annotation { "Feature Type Name" : "Feature", "Feature Type Description" : "" }
export const myFeature = defineFeature(function(context is Context, id is Id, definition is map)
    precondition{}
    {
        {
            var Q0;
            Q0=qCreatedBy(makeId("Top.planeOp"),FACE);
            var sketch = newSketch(context, id + "F0", { "sketchPlane" : qUnion([Q0])});
            skLineSegment(sketch, "E0.bottom", {"start": v(112.5, -12.5) * mm, "end": v(-112.5, -12.5) * mm});
            skLineSegment(sketch, "E0.top", {"start": v(112.5, 12.5) * mm, "end": v(-112.5, 12.5) * mm});
            skLineSegment(sketch, "E0.left", {"start": v(112.5, -12.5) * mm, "end": v(112.5, 12.5) * mm});
            skLineSegment(sketch, "E0.right", {"start": v(-112.5, -12.5) * mm, "end": v(-112.5, 12.5) * mm});
            skText(sketch, "E1", { "text": "Joseph Schmitz", "fontName": "RobotoSlab-Bold.ttf"});
            skPoint(sketch, "E2", {"position": v(-34.31, 0) * mm});
            skPoint(sketch, "E3", {"position": v(0, -12.5) * mm});
            skLineSegment(sketch, "E4", {"start": v(91.36, 3.09) * mm, "end": v(97.96, 10.26) * mm});
            skLineSegment(sketch, "E5", {"start": v(97.96, 10.26) * mm, "end": v(96.05, 3.1) * mm});
            skLineSegment(sketch, "E6", {"start": v(96.05, 3.1) * mm, "end": v(104.2, 3.1) * mm});
            skLineSegment(sketch, "E7", {"start": v(104.2, 3.1) * mm, "end": v(94.83, -1.5) * mm});
            skLineSegment(sketch, "E8", {"start": v(94.43, -1.04) * mm, "end": v(95.04, 2.05) * mm});
            skLineSegment(sketch, "E9", {"start": v(95.04, 2.05) * mm, "end": v(91.13, 2.15) * mm});
            skLineSegment(sketch, "E10", {"start": v(95.94, 6.62) * mm, "end": v(95.24, 3.1) * mm});
            skLineSegment(sketch, "E11", {"start": v(95.24, 3.1) * mm, "end": v(92.14, 3.09) * mm});
            skLineSegment(sketch, "E12", {"start": v(92.14, 3.09) * mm, "end": v(95.94, 6.62) * mm});
            skLineSegment(sketch, "E13", {"start": v(95.77, 2.03) * mm, "end": v(99.85, 1.91) * mm});
            skLineSegment(sketch, "E14", {"start": v(99.85, 1.91) * mm, "end": v(95.05, -0.7) * mm});
            skLineSegment(sketch, "E15", {"start": v(95.05, -0.7) * mm, "end": v(95.77, 2.03) * mm});
            skLineSegment(sketch, "E16", {"start": v(97.96, 10.26) * mm, "end": v(95.94, 6.62) * mm, "construction": true});
            skText(sketch, "E17", { "text": "121-D", "fontName": "RobotoSlab-Bold.ttf"});
            skPoint(sketch, "E18", {"position": v(92.9, -8.75) * mm});
            skPoint(sketch, "E19", {"position": v(81.54, -8.05) * mm});
            skPoint(sketch, "E20", {"position": v(86.8, -1.87) * mm});
            skPoint(sketch, "E21", {"position": v(59.08, 3.04) * mm});
            skLineSegment(sketch, "E22", {"start": v(94.83, -1.5) * mm, "end": v(92.9, -8.75) * mm});
            skLineSegment(sketch, "E23", {"start": v(94.43, -1.04) * mm, "end": v(81.54, -8.05) * mm});
            skLineSegment(sketch, "E24", {"start": v(86.8, -1.87) * mm, "end": v(91.13, 2.15) * mm});
            skLineSegment(sketch, "E25", {"start": v(59.08, 3.04) * mm, "end": v(91.36, 3.09) * mm});
            skLineSegment(sketch, "E26", {"start": v(59.08, 3.04) * mm, "end": v(59.07, 2.64) * mm});
            skLineSegment(sketch, "E27", {"start": v(59.07, 2.64) * mm, "end": v(90.4, 2.15) * mm});
            skLineSegment(sketch, "E28", {"start": v(86.8, -1.87) * mm, "end": v(86.53, -1.58) * mm});
            skLineSegment(sketch, "E29", {"start": v(86.53, -1.58) * mm, "end": v(91.36, 3.09) * mm, "construction": true});
            skLineSegment(sketch, "E30", {"start": v(86.53, -1.58) * mm, "end": v(90.4, 2.15) * mm});
            skLineSegment(sketch, "E31", {"start": v(81.54, -8.05) * mm, "end": v(81.73, -8.4) * mm});
            skLineSegment(sketch, "E32", {"start": v(92.9, -8.75) * mm, "end": v(92.52, -8.65) * mm});
            skLineSegment(sketch, "E33", {"start": v(81.73, -8.4) * mm, "end": v(94.83, -1.5) * mm, "construction": true});
            skLineSegment(sketch, "E34", {"start": v(92.52, -8.65) * mm, "end": v(94.43, -1.04) * mm, "construction": true});
            skLineSegment(sketch, "E35", {"start": v(81.73, -8.4) * mm, "end": v(94.23, -1.82) * mm});
            skLineSegment(sketch, "E36", {"start": v(94.23, -1.82) * mm, "end": v(92.52, -8.65) * mm});
            const initialGuessF0  = {"E1": [-0.1025, -0.0065, 1, 0, 0.013], "E17": [0.04787, -0.0095, 1, 0, 0.009]};
            skSetInitialGuess(sketch, initialGuessF0);
            skSolve(sketch);
        }
        {
            var Q0;
            Q0=makeQuery(id+"F0.imprint","IMPRINT",FACE,{"disambiguationData":[TD([[makeQuery(id+"F0.imprint","IMPRINT",EDGE,{"derivedFrom":sQuery(id+"F0.wireOp",EDGE,"E0.bottom")}),-1.0]])]});
            var Q1;
            Q1=makeQuery(id+"F0.imprint","IMPRINT",FACE,{"disambiguationData":[TD([[makeQuery(id+"F0.imprint","IMPRINT",EDGE,{"derivedFrom":sQuery(id+"F0.wireOp",EDGE,"E1.sketch_text.stroke-112")}),1.0]])]});
            var Q2;
            Q2=makeQuery(id+"F0.imprint","IMPRINT",FACE,{"disambiguationData":[TD([[makeQuery(id+"F0.imprint","IMPRINT",EDGE,{"derivedFrom":sQuery(id+"F0.wireOp",EDGE,"E1.sketch_text.stroke-85")}),1.0]])]});
            var Q3;
            Q3=makeQuery(id+"F0.imprint","IMPRINT",FACE,{"disambiguationData":[TD([[makeQuery(id+"F0.imprint","IMPRINT",EDGE,{"derivedFrom":sQuery(id+"F0.wireOp",EDGE,"E1.sketch_text.stroke-28")}),1.0]])]});
            var Q4;
            Q4=makeQuery(id+"F0.imprint","IMPRINT",FACE,{"disambiguationData":[TD([[makeQuery(id+"F0.imprint","IMPRINT",EDGE,{"derivedFrom":sQuery(id+"F0.wireOp",EDGE,"E13")}),-1.0]])]});
            var Q5;
            Q5=makeQuery(id+"F0.imprint","IMPRINT",FACE,{"disambiguationData":[TD([[makeQuery(id+"F0.imprint","IMPRINT",EDGE,{"derivedFrom":sQuery(id+"F0.wireOp",EDGE,"E10")}),-1.0]])]});
            var Q6;
            Q6=makeQuery(id+"F0.imprint","IMPRINT",FACE,{"disambiguationData":[TD([[makeQuery(id+"F0.imprint","IMPRINT",EDGE,{"derivedFrom":sQuery(id+"F0.wireOp",EDGE,"E17.sketch_text.stroke-60")}),1.0]])]});
            extrude(context, id + "F1", {"entities" : qUnion([Q0, Q1, Q2, Q3, Q4, Q5, Q6]), "depth" : (0.3 + .2 + .2) * mm});
        }
        {
            var Q0;
            Q0=makeQuery(id+"F0.imprint","IMPRINT",FACE,{"disambiguationData":[TD([[makeQuery(id+"F0.imprint","IMPRINT",EDGE,{"derivedFrom":sQuery(id+"F0.wireOp",EDGE,"E1.sketch_text.stroke-227")}),-1.0]])]});
            var Q1;
            Q1=makeQuery(id+"F0.imprint","IMPRINT",FACE,{"disambiguationData":[TD([[makeQuery(id+"F0.imprint","IMPRINT",EDGE,{"derivedFrom":sQuery(id+"F0.wireOp",EDGE,"E1.sketch_text.stroke-280")}),-1.0]])]});
            var Q2;
            Q2=makeQuery(id+"F0.imprint","IMPRINT",FACE,{"disambiguationData":[TD([[makeQuery(id+"F0.imprint","IMPRINT",EDGE,{"derivedFrom":sQuery(id+"F0.wireOp",EDGE,"E1.sketch_text.stroke-270")}),-1.0]])]});
            var Q3;
            Q3=makeQuery(id+"F0.imprint","IMPRINT",FACE,{"disambiguationData":[TD([[makeQuery(id+"F0.imprint","IMPRINT",EDGE,{"derivedFrom":sQuery(id+"F0.wireOp",EDGE,"E1.sketch_text.stroke-284")}),-1.0]])]});
            var Q4;
            Q4=makeQuery(id+"F0.imprint","IMPRINT",FACE,{"disambiguationData":[TD([[makeQuery(id+"F0.imprint","IMPRINT",EDGE,{"derivedFrom":sQuery(id+"F0.wireOp",EDGE,"E1.sketch_text.stroke-304")}),-1.0]])]});
            var Q5;
            Q5=makeQuery(id+"F0.imprint","IMPRINT",FACE,{"disambiguationData":[TD([[makeQuery(id+"F0.imprint","IMPRINT",EDGE,{"derivedFrom":sQuery(id+"F0.wireOp",EDGE,"E17.sketch_text.stroke-0")}),-1.0]])]});
            var Q6;
            Q6=makeQuery(id+"F0.imprint","IMPRINT",FACE,{"disambiguationData":[TD([[makeQuery(id+"F0.imprint","IMPRINT",EDGE,{"derivedFrom":sQuery(id+"F0.wireOp",EDGE,"E17.sketch_text.stroke-10")}),-1.0]])]});
            var Q7;
            Q7=makeQuery(id+"F0.imprint","IMPRINT",FACE,{"disambiguationData":[TD([[makeQuery(id+"F0.imprint","IMPRINT",EDGE,{"derivedFrom":sQuery(id+"F0.wireOp",EDGE,"E17.sketch_text.stroke-33")}),-1.0]])]});
            var Q8;
            Q8=makeQuery(id+"F0.imprint","IMPRINT",FACE,{"disambiguationData":[TD([[makeQuery(id+"F0.imprint","IMPRINT",EDGE,{"derivedFrom":sQuery(id+"F0.wireOp",EDGE,"E17.sketch_text.stroke-43")}),-1.0]])]});
            var Q9;
            Q9=makeQuery(id+"F0.imprint","IMPRINT",FACE,{"disambiguationData":[TD([[makeQuery(id+"F0.imprint","IMPRINT",EDGE,{"derivedFrom":sQuery(id+"F0.wireOp",EDGE,"E17.sketch_text.stroke-47")}),-1.0]])]});
            var Q10;
            Q10=makeQuery(id+"F0.imprint","IMPRINT",FACE,{"disambiguationData":[TD([[makeQuery(id+"F0.imprint","IMPRINT",EDGE,{"derivedFrom":sQuery(id+"F0.wireOp",EDGE,"66f59e6f-d666-4f71-bfd4-2eef0c262501")}),-1.0]])]});
            var Q11;
            Q11=makeQuery(id+"F0.imprint","IMPRINT",FACE,{"disambiguationData":[TD([[makeQuery(id+"F0.imprint","IMPRINT",EDGE,{"derivedFrom":sQuery(id+"F0.wireOp",EDGE,"E1.sketch_text.stroke-0")}),-1.0]])]});
            var Q12;
            Q12=makeQuery(id+"F0.imprint","IMPRINT",FACE,{"disambiguationData":[TD([[makeQuery(id+"F0.imprint","IMPRINT",EDGE,{"derivedFrom":sQuery(id+"F0.wireOp",EDGE,"E1.sketch_text.stroke-18")}),-1.0]])]});
            var Q13;
            Q13=makeQuery(id+"F0.imprint","IMPRINT",FACE,{"disambiguationData":[TD([[makeQuery(id+"F0.imprint","IMPRINT",EDGE,{"derivedFrom":sQuery(id+"F0.wireOp",EDGE,"E1.sketch_text.stroke-38")}),-1.0]])]});
            var Q14;
            Q14=makeQuery(id+"F0.imprint","IMPRINT",FACE,{"disambiguationData":[TD([[makeQuery(id+"F0.imprint","IMPRINT",EDGE,{"derivedFrom":sQuery(id+"F0.wireOp",EDGE,"E1.sketch_text.stroke-68")}),-1.0]])]});
            var Q15;
            Q15=makeQuery(id+"F0.imprint","IMPRINT",FACE,{"disambiguationData":[TD([[makeQuery(id+"F0.imprint","IMPRINT",EDGE,{"derivedFrom":sQuery(id+"F0.wireOp",EDGE,"E1.sketch_text.stroke-92")}),-1.0]])]});
            var Q16;
            Q16=makeQuery(id+"F0.imprint","IMPRINT",FACE,{"disambiguationData":[TD([[makeQuery(id+"F0.imprint","IMPRINT",EDGE,{"derivedFrom":sQuery(id+"F0.wireOp",EDGE,"E1.sketch_text.stroke-122")}),-1.0]])]});
            var Q17;
            Q17=makeQuery(id+"F0.imprint","IMPRINT",FACE,{"disambiguationData":[TD([[makeQuery(id+"F0.imprint","IMPRINT",EDGE,{"derivedFrom":sQuery(id+"F0.wireOp",EDGE,"E1.sketch_text.stroke-148")}),-1.0]])]});
            var Q18;
            Q18=makeQuery(id+"F0.imprint","IMPRINT",FACE,{"disambiguationData":[TD([[makeQuery(id+"F0.imprint","IMPRINT",EDGE,{"derivedFrom":sQuery(id+"F0.wireOp",EDGE,"E1.sketch_text.stroke-178")}),-1.0]])]});
            var Q19;
            Q19=makeQuery(id+"F0.imprint","IMPRINT",FACE,{"disambiguationData":[TD([[makeQuery(id+"F0.imprint","IMPRINT",EDGE,{"derivedFrom":sQuery(id+"F0.wireOp",EDGE,"E1.sketch_text.stroke-201")}),-1.0]])]});
            var Q20;
            Q20=makeQuery(id+"F0.imprint","IMPRINT",FACE,{"disambiguationData":[TD([[makeQuery(id+"F0.imprint","IMPRINT",EDGE,{"derivedFrom":sQuery(id+"F0.wireOp",EDGE,"E4")}),-1.0]])]});
            extrude(context, id + "F2", {"entities" : qUnion([Q0, Q1, Q2, Q3, Q4, Q5, Q6, Q7, Q8, Q9, Q10, Q11, Q12, Q13, Q14, Q15, Q16, Q17, Q18, Q19, Q20]), "depth" : 8 * mm});
        }
        {
            var Q0;
            Q0=qCreatedBy(makeId("Top.planeOp"),FACE);
            var sketch = newSketch(context, id + "F3", { "sketchPlane" : qUnion([Q0])});
            skLineSegment(sketch, "E37.bottom", {"start": v(-112.5, 12.5) * mm, "end": v(-37.5, 12.5) * mm});
            skLineSegment(sketch, "E37.top", {"start": v(-112.5, -12.5) * mm, "end": v(-37.5, -12.5) * mm});
            skLineSegment(sketch, "E37.left", {"start": v(-112.5, 12.5) * mm, "end": v(-112.5, -12.5) * mm});
            skLineSegment(sketch, "E37.right", {"start": v(-37.5, 12.5) * mm, "end": v(-37.5, -12.5) * mm});
            skLineSegment(sketch, "E38.bottom", {"start": v(-37.5, 12.5) * mm, "end": v(37.5, 12.5) * mm});
            skLineSegment(sketch, "E38.top", {"start": v(-37.5, -12.5) * mm, "end": v(37.5, -12.5) * mm});
            skLineSegment(sketch, "E38.right", {"start": v(37.5, 12.5) * mm, "end": v(37.5, -12.5) * mm});
            skLineSegment(sketch, "E39.bottom", {"start": v(37.5, 12.5) * mm, "end": v(112.5, 12.5) * mm});
            skLineSegment(sketch, "E39.top", {"start": v(37.5, -12.5) * mm, "end": v(112.5, -12.5) * mm});
            skLineSegment(sketch, "E39.right", {"start": v(112.5, 12.5) * mm, "end": v(112.5, -12.5) * mm});
            skSolve(sketch);
        }
        {
            var Q0;
            Q0=makeQuery(id+"F3.imprint","IMPRINT",FACE,{"disambiguationData":[TD([[makeQuery(id+"F3.imprint","IMPRINT",EDGE,{"derivedFrom":sQuery(id+"F3.wireOp",EDGE,"E38.bottom")}),-1.0]])]});
            var Q1;
            Q1=makeQuery(id+"F3.imprint","IMPRINT",FACE,{"disambiguationData":[TD([[makeQuery(id+"F3.imprint","IMPRINT",EDGE,{"derivedFrom":sQuery(id+"F3.wireOp",EDGE,"E37.bottom")}),-1.0]])]});
            extrude(context, id + "F4", {"entities" : qUnion([Q0, Q1]), "operationType" : NewBodyOperationType.REMOVE, "depth" : 25 * mm});
        }
    });